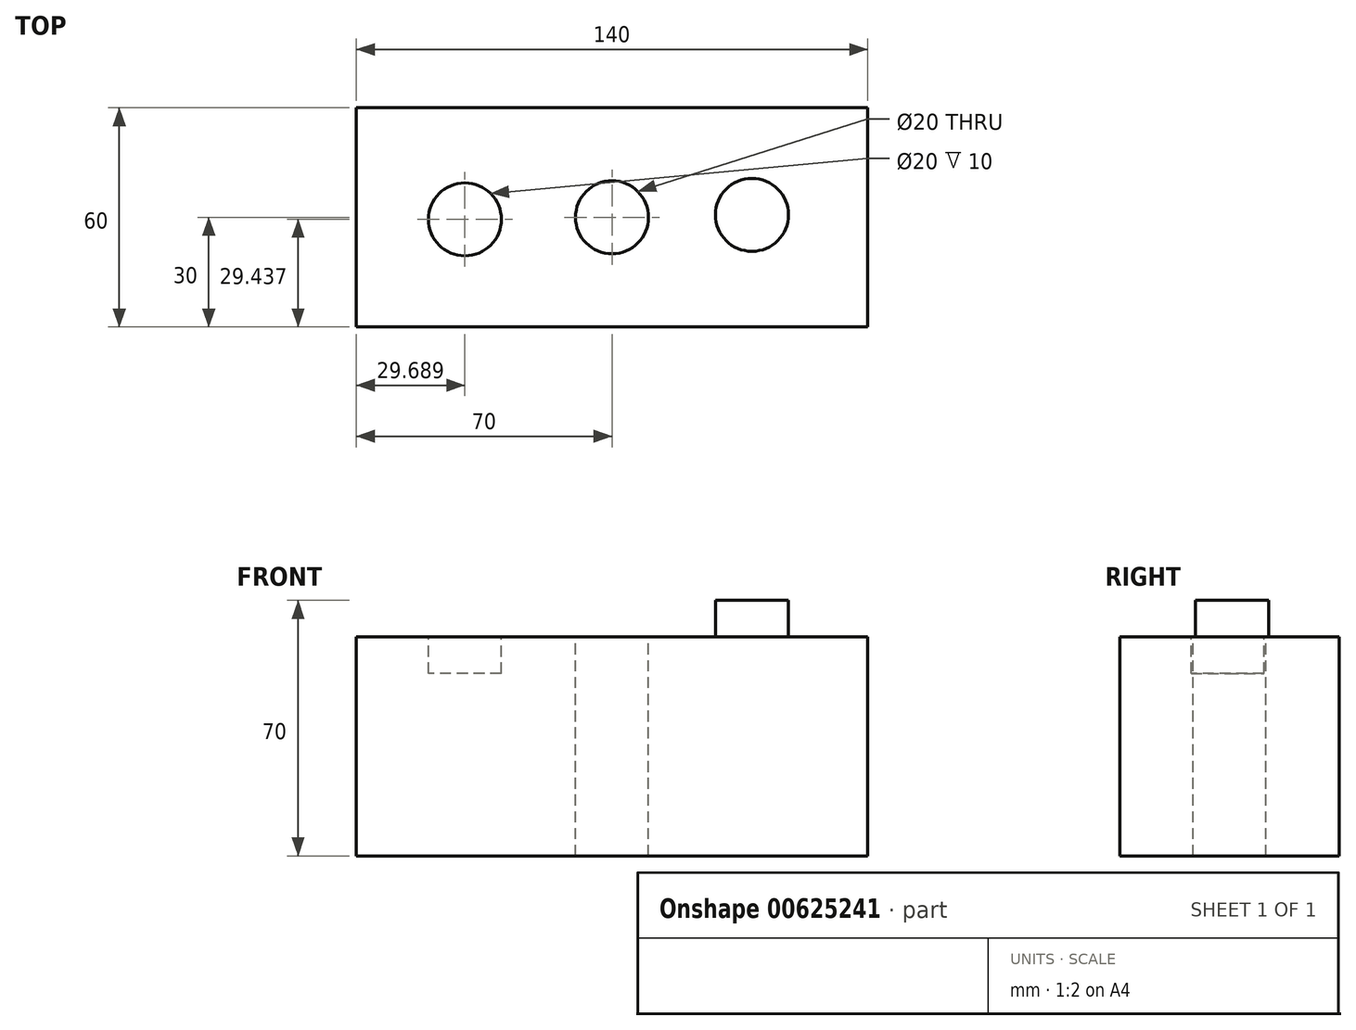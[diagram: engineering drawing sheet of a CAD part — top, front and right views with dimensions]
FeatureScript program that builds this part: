
annotation { "Feature Type Name" : "Feature", "Feature Type Description" : "" }
export const myFeature = defineFeature(function(context is Context, id is Id, definition is map)
    precondition{}
    {
        {
            var Q0;
            Q0=qCreatedBy(makeId("Top.planeOp"),FACE);
            var sketch = newSketch(context, id + "F0", { "sketchPlane" : qUnion([Q0])});
            skLineSegment(sketch, "E0.bottom", {"start": v(70, -30) * mm, "end": v(-70, -30) * mm});
            skLineSegment(sketch, "E0.top", {"start": v(70, 30) * mm, "end": v(-70, 30) * mm});
            skLineSegment(sketch, "E0.left", {"start": v(70, -30) * mm, "end": v(70, 30) * mm});
            skLineSegment(sketch, "E0.right", {"start": v(-70, -30) * mm, "end": v(-70, 30) * mm});
            skPoint(sketch, "E0.middle", {"position": v(0, 0) * mm});
            skSolve(sketch);
        }
        {
            var Q0;
            Q0 = qSketchRegion(id + "F0", true);
            extrude(context, id + "F1", {"entities" : qUnion([Q0]), "depth" : 60 * mm, "offsetDistance" : 25 * mm});
        }
        {
            var Q0;
            Q0=makeQuery(id+"F1.opExtrude","CAP_FACE",FACE,{"disambiguationData":[OSD([sQuery(id+"F0.wireOp",EDGE,"E0.bottom"),sQuery(id+"F0.wireOp",EDGE,"E0.top"),sQuery(id+"F0.wireOp",EDGE,"E0.left"),sQuery(id+"F0.wireOp",EDGE,"E0.right")])],"isStart":false});
            var sketch = newSketch(context, id + "F2", { "sketchPlane" : qUnion([Q0])});
            skLineSegment(sketch, "E1", {"start": v(-70, 0) * mm, "end": v(-50, 0) * mm});
            skPoint(sketch, "E1.endSnap0", {"position": v(-70, 0) * mm});
            skSolve(sketch);
        }
        {
            var Q0;
            {var subQ1=makeQuery(id+"F1.opExtrude","CAP_EDGE",EDGE,{"disambiguationData":[OSD([sQuery(id+"F0.wireOp",EDGE,"E0.bottom")])],"isStart":false});Q0=makeQuery(id+"F2.imprint","IMPRINT",FACE,{"disambiguationData":[TD([[makeQuery(id+"F2.imprint","IMPRINT",EDGE,{"derivedFrom":subQ1}),-1.0]])]});}
            var sketch = newSketch(context, id + "F3", { "sketchPlane" : qUnion([Q0])});
            skCircle(sketch, "E2", {"center": v(-40.31, -0.56) * mm, "radius": 10 * mm});
            skPoint(sketch, "E2.first.point", {"position": v(-50.3, 0) * mm});
            skPoint(sketch, "E2.second.point", {"position": v(-30.33, 0) * mm});
            skPoint(sketch, "E2.third.point", {"position": v(-38.31, 9.24) * mm});
            skSolve(sketch);
        }
        {
            var Q0;
            {var subQ1=makeQuery(id+"F1.opExtrude","CAP_EDGE",EDGE,{"disambiguationData":[OSD([sQuery(id+"F0.wireOp",EDGE,"E0.bottom")])],"isStart":false});Q0=makeQuery(id+"F2.imprint","IMPRINT",FACE,{"disambiguationData":[TD([[makeQuery(id+"F2.imprint","IMPRINT",EDGE,{"derivedFrom":subQ1}),-1.0]])]});}
            var sketch = newSketch(context, id + "F4", { "sketchPlane" : qUnion([Q0])});
            skCircle(sketch, "E3", {"center": v(0, 0) * mm, "radius": 10 * mm});
            skSolve(sketch);
        }
        {
            var Q0;
            {var subQ1=makeQuery(id+"F1.opExtrude","CAP_EDGE",EDGE,{"disambiguationData":[OSD([sQuery(id+"F0.wireOp",EDGE,"E0.bottom")])],"isStart":false});Q0=makeQuery(id+"F2.imprint","IMPRINT",FACE,{"disambiguationData":[TD([[makeQuery(id+"F2.imprint","IMPRINT",EDGE,{"derivedFrom":subQ1}),-1.0]])]});}
            var sketch = newSketch(context, id + "F5", { "sketchPlane" : qUnion([Q0])});
            skCircle(sketch, "E4", {"center": v(38.33, 0.68) * mm, "radius": 10 * mm});
            skPoint(sketch, "E4.first.point", {"position": v(48.3, 0) * mm});
            skPoint(sketch, "E4.second.point", {"position": v(28.35, 0) * mm});
            skPoint(sketch, "E4.third.point", {"position": v(39.54, -9.25) * mm});
            skSolve(sketch);
        }
        {
            var Q0;
            Q0 = qSketchRegion(id + "F5", true);
            extrude(context, id + "F6", {"entities" : qUnion([Q0]), "operationType" : NewBodyOperationType.ADD, "depth" : 10 * mm, "offsetDistance" : 25 * mm});
        }
        {
            var Q0;
            Q0 = qSketchRegion(id + "F4", true);
            extrude(context, id + "F7", {"entities" : qUnion([Q0]), "operationType" : NewBodyOperationType.REMOVE, "oppositeDirection" : true, "depth" : 105.8 * mm, "offsetDistance" : 25 * mm});
        }
        {
            var Q0;
            Q0 = qSketchRegion(id + "F3", true);
            extrude(context, id + "F8", {"entities" : qUnion([Q0]), "operationType" : NewBodyOperationType.REMOVE, "oppositeDirection" : true, "depth" : 10 * mm, "offsetDistance" : 25 * mm});
        }
    });
